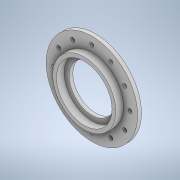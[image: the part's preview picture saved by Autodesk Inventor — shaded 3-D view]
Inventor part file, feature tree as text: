
AUTODESK INVENTOR PART (.ipt)
format: ipt  version: 2020 (Build 240168000, 168)  size: 157,184 bytes
history: native  units: in
note: dims shown in document units (in); Inventor stores cm internally (conversion verified against a paired STEP export)
features: extrude x2, sketch x2
ambient origin geometry x8: Origin, YZ Plane, XZ Plane, XY Plane, X Axis, Y Axis, Z Axis, Center Point
bodies: Solid1 (feature_tree)
feature tree (4):
  extrude  "Extrusion1"  Depth=2.5in
  extrude  "Extrusion2"  Depth=3.0in
  sketch  "Sketch1"  dims[d0=2.5in d1=6.0in]
  sketch  "Sketch2"  dims[d2=0.2656in d3=3.0in d4=4.7244in d6=360.0deg d8=0.25in d9=0.0in d10=3.6407in d11=0.25in d12=0.5in d13=0.0in]
